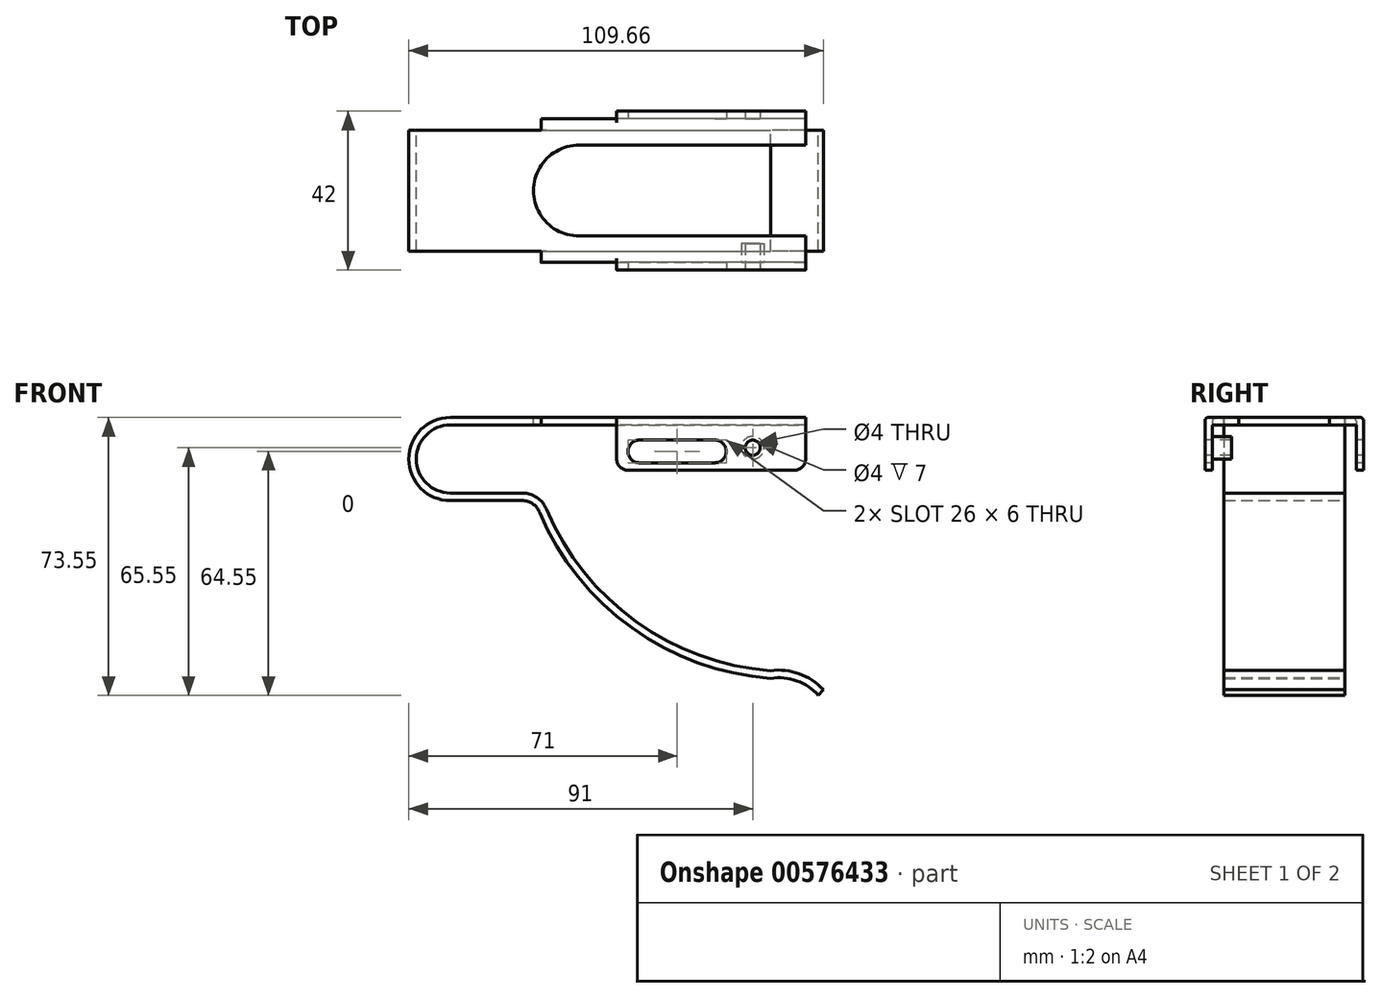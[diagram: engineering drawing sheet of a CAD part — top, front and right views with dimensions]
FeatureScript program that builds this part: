
annotation { "Feature Type Name" : "Feature", "Feature Type Description" : "" }
export const myFeature = defineFeature(function(context is Context, id is Id, definition is map)
    precondition{}
    {
        {
            var Q0;
            Q0=qCreatedBy(makeId("Front.planeOp"),FACE);
            var sketch = newSketch(context, id + "F0", { "sketchPlane" : qUnion([Q0])});
            skArc(sketch, "E0", {"start": v(0, 11) * mm, "mid": v(-11, 0) * mm, "end": v(0, -11) * mm});
            skLineSegment(sketch, "E1", {"start": v(0, 11) * mm, "end": v(94, 11) * mm});
            skLineSegment(sketch, "E2", {"start": v(0, -11) * mm, "end": v(19, -11) * mm});
            skArc(sketch, "E3", {"start": v(23.61, -14.06) * mm, "mid": v(47.99, -44.67) * mm, "end": v(84.77, -58.01) * mm});
            skArc(sketch, "E4", {"start": v(97.36, -62.55) * mm, "mid": v(91.65, -58.68) * mm, "end": v(84.77, -58.01) * mm});
            skPoint(sketch, "E5.visualSharp", {"position": v(22.4, -11) * mm});
            skArc(sketch, "E5.filletArc", {"start": v(23.61, -14.06) * mm, "mid": v(21.77, -11.84) * mm, "end": v(19, -11) * mm});
            skLineSegment(sketch, "E6.0", {"start": v(0, 9) * mm, "end": v(94, 9) * mm});
            skArc(sketch, "E6.1", {"start": v(0, 9) * mm, "mid": v(-9, 0) * mm, "end": v(0, -9) * mm});
            skArc(sketch, "E6.2", {"start": v(98.66, -61) * mm, "mid": v(92.3, -56.79) * mm, "end": v(84.7, -56) * mm});
            skArc(sketch, "E6.3", {"start": v(25.45, -13.3) * mm, "mid": v(49.07, -42.99) * mm, "end": v(84.7, -56) * mm});
            skArc(sketch, "E6.4", {"start": v(25.45, -13.3) * mm, "mid": v(22.88, -10.17) * mm, "end": v(19, -9) * mm});
            skLineSegment(sketch, "E6.5", {"start": v(0, -9) * mm, "end": v(19, -9) * mm});
            skLineSegment(sketch, "E7", {"start": v(94, 11) * mm, "end": v(94, 9) * mm});
            skLineSegment(sketch, "E8", {"start": v(98.66, -61) * mm, "end": v(97.36, -62.55) * mm});
            skLineSegment(sketch, "E9", {"start": v(98.66, -61) * mm, "end": v(103.75, -61) * mm, "construction": true});
            skSolve(sketch);
        }
        {
            var Q0;
            Q0 = qSketchRegion(id + "F0", true);
            extrude(context, id + "F1", {"entities" : qUnion([Q0]), "depth" : 16 * mm, "offsetDistance" : 25 * mm});
        }
        {
            var Q0;
            Q0=makeQuery(id+"F1.opExtrude","SWEPT_FACE",FACE,{"disambiguationData":[OSD([sQuery(id+"F0.wireOp",EDGE,"E1")])]});
            var sketch = newSketch(context, id + "F2", { "sketchPlane" : qUnion([Q0])});
            skLineSegment(sketch, "E10", {"start": v(94, -16) * mm, "end": v(94, -19) * mm});
            skLineSegment(sketch, "E11", {"start": v(94, -19) * mm, "end": v(24, -19) * mm});
            skLineSegment(sketch, "E12", {"start": v(24, -19) * mm, "end": v(24, -16) * mm});
            skPoint(sketch, "E12.endSnap0", {"position": v(47, -16) * mm});
            skSolve(sketch);
        }
        {
            var Q0;
            {var subQ0=sQuery(id+"F2.wireOp",EDGE,"E10");Q0=makeQuery(id+"F2.imprint","IMPRINT",FACE,{"disambiguationData":[TD([[makeQuery(id+"F2.imprint","IMPRINT",EDGE,{"derivedFrom":subQ0}),-1.0]])]});}
            extrude(context, id + "F3", {"entities" : qUnion([Q0]), "operationType" : NewBodyOperationType.ADD, "oppositeDirection" : true, "depth" : 2 * mm, "offsetDistance" : 25 * mm});
        }
        {
            var Q0;
            Q0=makeQuery(id+"F3.opExtrude","SWEPT_FACE",FACE,{"disambiguationData":[OSD([sQuery(id+"F2.wireOp",EDGE,"E11")])]});
            var sketch = newSketch(context, id + "F4", { "sketchPlane" : qUnion([Q0])});
            skLineSegment(sketch, "E13.bottom", {"start": v(94, 11) * mm, "end": v(44, 11) * mm});
            skLineSegment(sketch, "E13.top", {"start": v(94, -3) * mm, "end": v(44, -3) * mm});
            skLineSegment(sketch, "E13.left", {"start": v(94, 11) * mm, "end": v(94, -3) * mm});
            skLineSegment(sketch, "E13.right", {"start": v(44, 11) * mm, "end": v(44, -3) * mm});
            skSolve(sketch);
        }
        {
            var Q0;
            Q0 = qSketchRegion(id + "F4", true);
            extrude(context, id + "F5", {"entities" : qUnion([Q0]), "operationType" : NewBodyOperationType.ADD, "depth" : 2 * mm, "offsetDistance" : 25 * mm});
        }
        {
            var Q0;
            Q0=makeQuery(id+"F5.opExtrude","CAP_EDGE",EDGE,{"disambiguationData":[OSD([sQuery(id+"F4.wireOp",EDGE,"E13.bottom")])],"isStart":false});
            var Q1;
            Q1=makeQuery(id+"F3.opExtrude","CAP_EDGE",EDGE,{"disambiguationData":[OSD([sQuery(id+"F2.wireOp",EDGE,"E11")])],"isStart":true});
            fillet(context, id + "F6", {"entities" : qUnion([Q0, Q1]), "radius" : 1 * mm, "allowEdgeOverflow" : false});
        }
        {
            var Q0;
            Q0=makeQuery(id+"F1.opExtrude","SWEPT_BODY",BODY,{"disambiguationData":[OSD([sQuery(id+"F0.wireOp",EDGE,"E0"),sQuery(id+"F0.wireOp",EDGE,"E1"),sQuery(id+"F0.wireOp",EDGE,"E2"),sQuery(id+"F0.wireOp",EDGE,"E3"),sQuery(id+"F0.wireOp",EDGE,"E4"),sQuery(id+"F0.wireOp",EDGE,"E5.filletArc"),sQuery(id+"F0.wireOp",EDGE,"E6.0"),sQuery(id+"F0.wireOp",EDGE,"E6.1"),sQuery(id+"F0.wireOp",EDGE,"E6.2"),sQuery(id+"F0.wireOp",EDGE,"E6.3"),sQuery(id+"F0.wireOp",EDGE,"E6.4"),sQuery(id+"F0.wireOp",EDGE,"E6.5"),sQuery(id+"F0.wireOp",EDGE,"E7"),sQuery(id+"F0.wireOp",EDGE,"E8")])]});
            var Q1;
            Q1=qCreatedBy(makeId("Front.planeOp"),FACE);
            mirror(context, id + "F7", {"operationType" : NewBodyOperationType.ADD, "entities" : qUnion([Q0]), "mirrorPlane" : qUnion([Q1])});
        }
        {
            var Q0;
            {var subQ0=sQuery(id+"F0.wireOp",EDGE,"E1");var subQ1=makeQuery(id+"F5.boolean.opBoolean","MERGE",FACE,{"derivedFrom":[makeQuery(id+"F3.boolean.opBoolean","MERGE",FACE,{"derivedFrom":[makeQuery(id+"F1.opExtrude","SWEPT_FACE",FACE,{"disambiguationData":[OSD([subQ0])]}),makeQuery(id+"F3.opExtrude","CAP_FACE",FACE,{"disambiguationData":[OSD([subQ0,sQuery(id+"F2.wireOp",EDGE,"E10"),sQuery(id+"F2.wireOp",EDGE,"E11"),sQuery(id+"F2.wireOp",EDGE,"E12")])],"isStart":true})]}),makeQuery(id+"F5.opExtrude","SWEPT_FACE",FACE,{"disambiguationData":[OSD([sQuery(id+"F4.wireOp",EDGE,"E13.bottom")])]})]});Q0=makeQuery(id+"F7.boolean.opBoolean","MERGE",FACE,{"derivedFrom":[subQ1,makeQuery(id+"F7.opPattern","COPY",FACE,{"derivedFrom":subQ1,"instanceName":"1"})]});}
            var sketch = newSketch(context, id + "F8", { "sketchPlane" : qUnion([Q0])});
            skArc(sketch, "E14", {"start": v(34.09, 12) * mm, "mid": v(22, 0) * mm, "end": v(34.1, -12) * mm});
            skLineSegment(sketch, "E15", {"start": v(34.09, 12) * mm, "end": v(94, 12) * mm});
            skLineSegment(sketch, "E16", {"start": v(34.1, -12) * mm, "end": v(94, -12) * mm});
            skLineSegment(sketch, "E17", {"start": v(94, -12) * mm, "end": v(94, 12) * mm});
            skSolve(sketch);
        }
        {
            var Q0;
            Q0 = qSketchRegion(id + "F8", true);
            extrude(context, id + "F9", {"entities" : qUnion([Q0]), "operationType" : NewBodyOperationType.REMOVE, "oppositeDirection" : true, "depth" : 2 * mm, "offsetDistance" : 25 * mm});
        }
        {
            var Q0;
            Q0=makeQuery(id+"F5.opExtrude","CAP_FACE",FACE,{"disambiguationData":[OSD([sQuery(id+"F4.wireOp",EDGE,"E13.bottom"),sQuery(id+"F4.wireOp",EDGE,"E13.top"),sQuery(id+"F4.wireOp",EDGE,"E13.left"),sQuery(id+"F4.wireOp",EDGE,"E13.right")])],"isStart":false});
            var sketch = newSketch(context, id + "F10", { "sketchPlane" : qUnion([Q0])});
            skLineSegment(sketch, "E18", {"start": v(50, 2) * mm, "end": v(70, 2) * mm});
            skArc(sketch, "E19.0.startCap", {"start": v(50, -1) * mm, "mid": v(47, 2) * mm, "end": v(50, 5) * mm});
            skArc(sketch, "E19.0.endCap", {"start": v(70, 5) * mm, "mid": v(73, 2) * mm, "end": v(70, -1) * mm});
            skLineSegment(sketch, "E19.0.left", {"start": v(50, 5) * mm, "end": v(70, 5) * mm});
            skLineSegment(sketch, "E19.0.right", {"start": v(50, -1) * mm, "end": v(70, -1) * mm});
            skSolve(sketch);
        }
        {
            var Q0;
            Q0 = qSketchRegion(id + "F10", true);
            extrude(context, id + "F11", {"entities" : qUnion([Q0]), "operationType" : NewBodyOperationType.REMOVE, "endBound" : BoundingType.THROUGH_ALL, "oppositeDirection" : true, "depth" : 25 * mm, "offsetDistance" : 25 * mm});
        }
        {
            var Q0;
            Q0=makeQuery(id+"F5.opExtrude","CAP_FACE",FACE,{"disambiguationData":[OSD([sQuery(id+"F4.wireOp",EDGE,"E13.bottom"),sQuery(id+"F4.wireOp",EDGE,"E13.top"),sQuery(id+"F4.wireOp",EDGE,"E13.left"),sQuery(id+"F4.wireOp",EDGE,"E13.right")])],"isStart":false});
            var sketch = newSketch(context, id + "F12", { "sketchPlane" : qUnion([Q0])});
            skPoint(sketch, "E20", {"position": v(80, 3) * mm});
            skSolve(sketch);
        }
        {
            var Q0;
            Q0=sQuery(id+"F12.wireOp",VERTEX,"E20");
            var Q1;
            Q1=makeQuery(id+"F1.opExtrude","SWEPT_BODY",BODY,{"disambiguationData":[OSD([sQuery(id+"F0.wireOp",EDGE,"E0"),sQuery(id+"F0.wireOp",EDGE,"E1"),sQuery(id+"F0.wireOp",EDGE,"E2"),sQuery(id+"F0.wireOp",EDGE,"E3"),sQuery(id+"F0.wireOp",EDGE,"E4"),sQuery(id+"F0.wireOp",EDGE,"E5.filletArc"),sQuery(id+"F0.wireOp",EDGE,"E6.0"),sQuery(id+"F0.wireOp",EDGE,"E6.1"),sQuery(id+"F0.wireOp",EDGE,"E6.2"),sQuery(id+"F0.wireOp",EDGE,"E6.3"),sQuery(id+"F0.wireOp",EDGE,"E6.4"),sQuery(id+"F0.wireOp",EDGE,"E6.5"),sQuery(id+"F0.wireOp",EDGE,"E7"),sQuery(id+"F0.wireOp",EDGE,"E8")])]});
            hole(context, id + "F13", {"style" : HoleStyle.SIMPLE, "endStyle" : HoleEndStyle.THROUGH, "holeDiameter" : 4 * mm, "majorDiameter" : 5 * mm, "isTappedThrough" : true, "tappedDepth" : 12 * mm, "tapClearance" : 3, "locations" : qUnion([Q0]), "scope" : qUnion([Q1])});
        }
        {
            var Q0;
            Q0=makeQuery(id+"F5.opExtrude","CAP_FACE",FACE,{"disambiguationData":[OSD([sQuery(id+"F4.wireOp",EDGE,"E13.bottom"),sQuery(id+"F4.wireOp",EDGE,"E13.top"),sQuery(id+"F4.wireOp",EDGE,"E13.left"),sQuery(id+"F4.wireOp",EDGE,"E13.right")])],"isStart":true});
            var sketch = newSketch(context, id + "F14", { "sketchPlane" : qUnion([Q0])});
            skCircle(sketch, "E21.0", {"center": v(-80, 3) * mm, "radius": 2 * mm});
            skCircle(sketch, "E22.0", {"center": v(-80, 3) * mm, "radius": 3 * mm});
            skSolve(sketch);
        }
        {
            var Q0;
            Q0 = qSketchRegion(id + "F14", true);
            extrude(context, id + "F15", {"entities" : qUnion([Q0]), "operationType" : NewBodyOperationType.ADD, "depth" : 5 * mm, "offsetDistance" : 25 * mm});
        }
        {
            var Q0;
            Q0=makeQuery(id+"F7.opPattern","COPY",EDGE,{"derivedFrom":makeQuery(id+"F5.opExtrude","SWEPT_EDGE",EDGE,{"disambiguationData":[OSD([sQuery(id+"F4.wireOp",EDGE,"E13.top"),sQuery(id+"F4.wireOp",EDGE,"E13.right")])]}),"instanceName":"1"});
            var Q1;
            Q1=makeQuery(id+"F7.opPattern","COPY",EDGE,{"derivedFrom":makeQuery(id+"F5.opExtrude","SWEPT_EDGE",EDGE,{"disambiguationData":[OSD([sQuery(id+"F4.wireOp",EDGE,"E13.top"),sQuery(id+"F4.wireOp",EDGE,"E13.left")])]}),"instanceName":"1"});
            var Q2;
            Q2=makeQuery(id+"F5.opExtrude","SWEPT_EDGE",EDGE,{"disambiguationData":[OSD([sQuery(id+"F4.wireOp",EDGE,"E13.top"),sQuery(id+"F4.wireOp",EDGE,"E13.left")])]});
            var Q3;
            Q3=makeQuery(id+"F5.opExtrude","SWEPT_EDGE",EDGE,{"disambiguationData":[OSD([sQuery(id+"F4.wireOp",EDGE,"E13.top"),sQuery(id+"F4.wireOp",EDGE,"E13.right")])]});
            fillet(context, id + "F16", {"entities" : qUnion([Q0, Q1, Q2, Q3]), "radius" : 3 * mm, "tangentPropagation" : true, "allowEdgeOverflow" : false});
        }
    });
